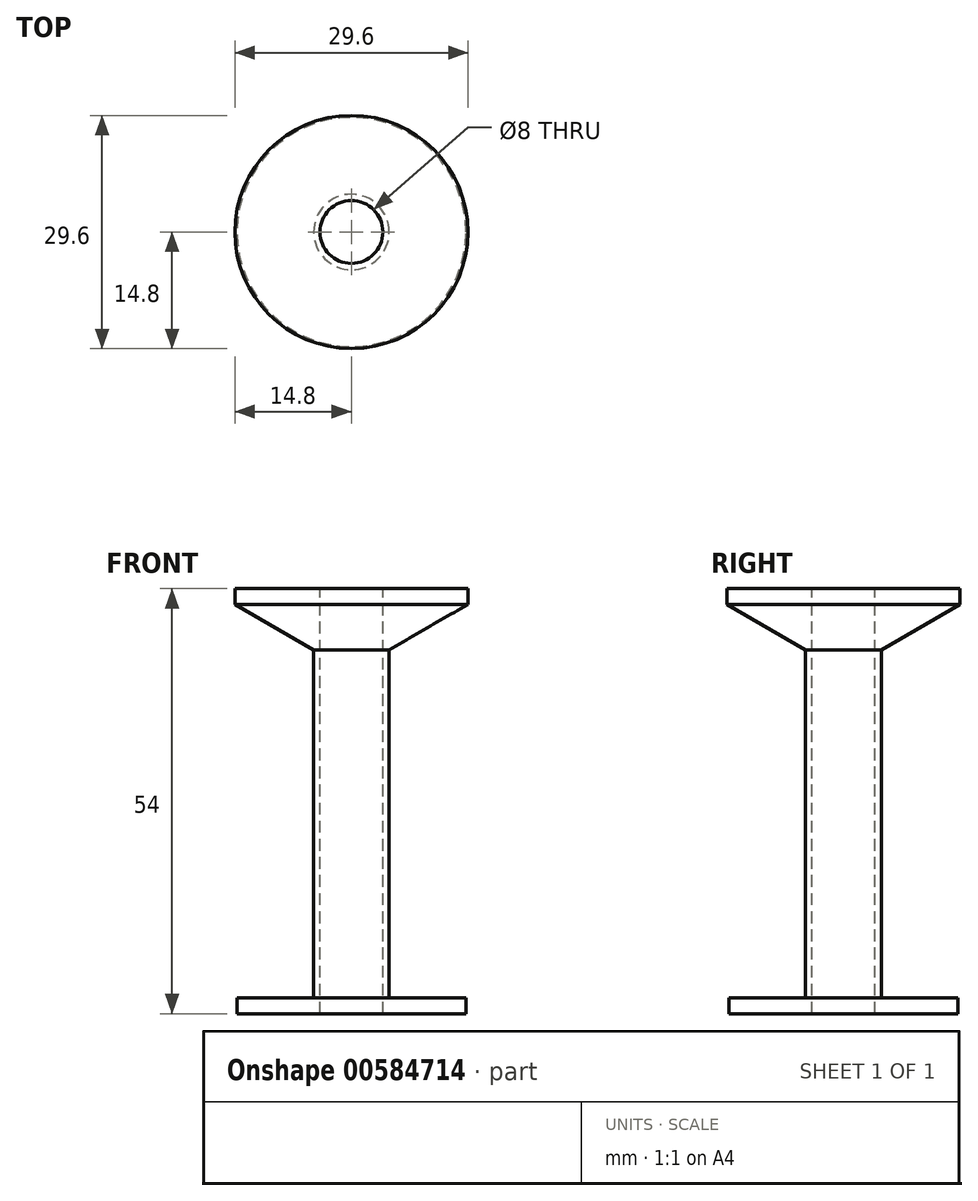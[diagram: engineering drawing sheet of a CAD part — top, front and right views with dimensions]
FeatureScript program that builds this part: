
annotation { "Feature Type Name" : "Feature", "Feature Type Description" : "" }
export const myFeature = defineFeature(function(context is Context, id is Id, definition is map)
    precondition{}
    {
        {
            var Q0;
            Q0=qCreatedBy(makeId("Front.planeOp"),FACE);
            var sketch = newSketch(context, id + "F0", { "sketchPlane" : qUnion([Q0])});
            skLineSegment(sketch, "E0", {"start": v(-4, 0) * mm, "end": v(-14.55, 0) * mm});
            skLineSegment(sketch, "E1", {"start": v(-14.55, 0) * mm, "end": v(-14.55, 2) * mm});
            skLineSegment(sketch, "E2", {"start": v(-14.55, 2) * mm, "end": v(-4.8, 2) * mm});
            skLineSegment(sketch, "E3", {"start": v(-4.8, 2) * mm, "end": v(-4.8, 52) * mm});
            skLineSegment(sketch, "E4", {"start": v(-4.8, 52) * mm, "end": v(-14.8, 52) * mm});
            skLineSegment(sketch, "E5", {"start": v(-14.8, 52) * mm, "end": v(-14.8, 54) * mm});
            skLineSegment(sketch, "E6", {"start": v(-14.8, 54) * mm, "end": v(-4, 54) * mm});
            skLineSegment(sketch, "E7", {"start": v(0, 54) * mm, "end": v(0, 0) * mm, "construction": true});
            skLineSegment(sketch, "E8", {"start": v(-4, 54) * mm, "end": v(-4, 0) * mm});
            skSolve(sketch);
        }
        {
            var Q0;
            Q0 = qSketchRegion(id + "F0", true);
            var Q1;
            Q1=sQuery(id+"F0.wireOp",EDGE,"E7");
            revolve(context, id + "F1", {"entities" : qUnion([Q0]), "axis" : qUnion([Q1]), "revolveType" : RevolveType.FULL});
        }
        {
            var Q0;
            Q0=makeQuery(id+"F1.opRevolve","SWEPT_EDGE",EDGE,{"disambiguationData":[OSD([sQuery(id+"F0.wireOp",EDGE,"E3"),sQuery(id+"F0.wireOp",EDGE,"E4")])]});
            chamfer(context, id + "F2", {"entities" : qUnion([Q0]), "chamferType" : ChamferType.OFFSET_ANGLE, "width" : 10 * mm, "oppositeDirection" : false, "angle" : 30 * degree, "tangentPropagation" : true});
        }
    });
